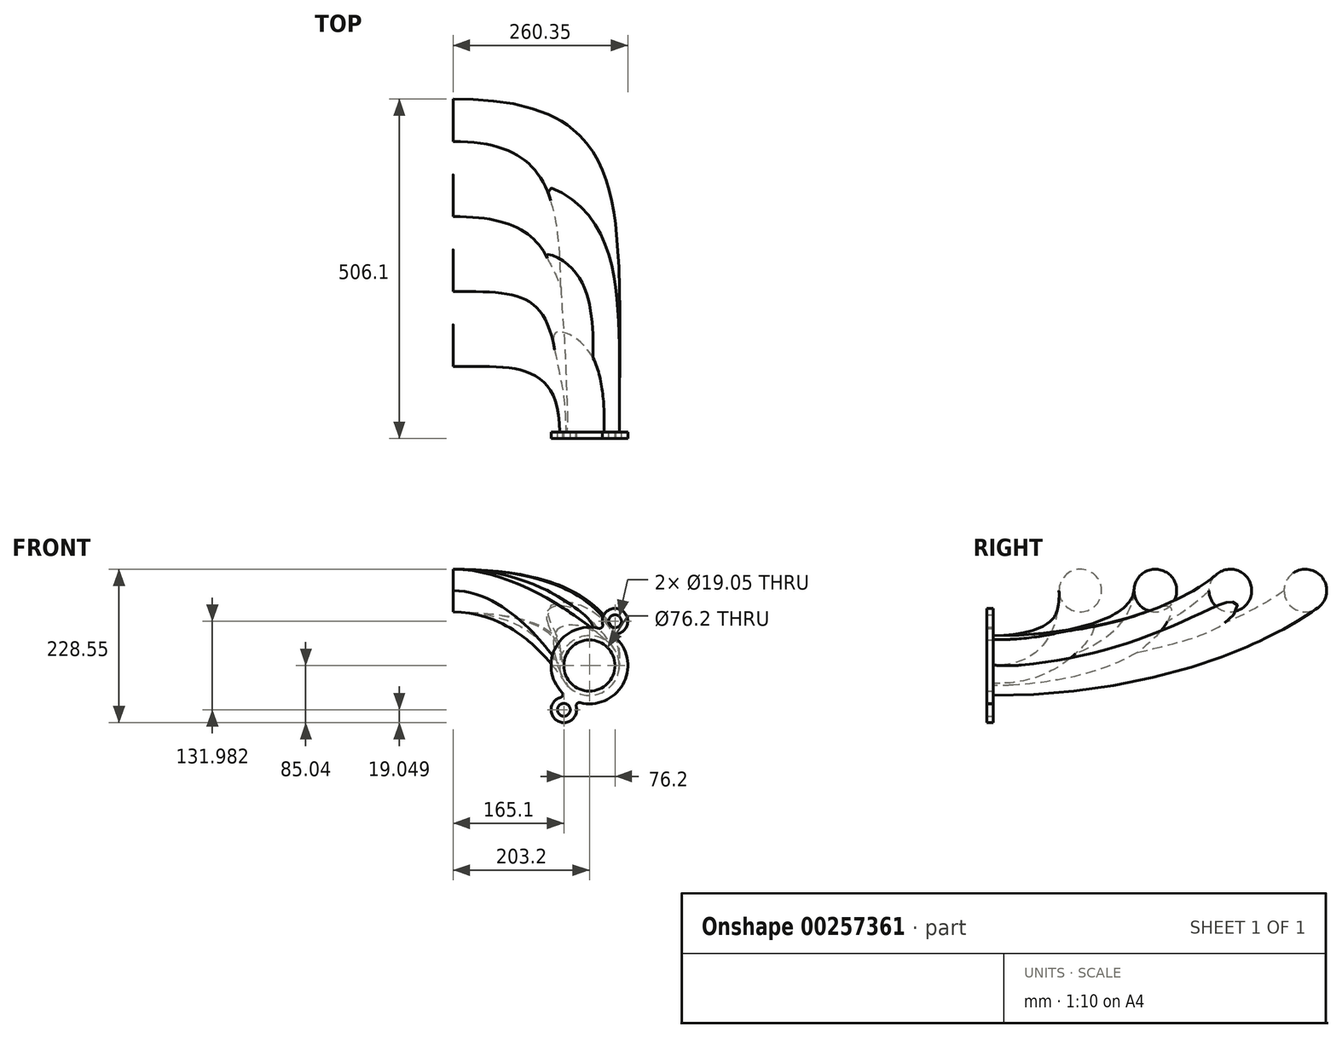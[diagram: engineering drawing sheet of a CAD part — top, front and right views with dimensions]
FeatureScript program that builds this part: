
annotation { "Feature Type Name" : "Feature", "Feature Type Description" : "" }
export const myFeature = defineFeature(function(context is Context, id is Id, definition is map)
    precondition{}
    {
        {
            var Q0;
            Q0=qCreatedBy(makeId("Right.planeOp"),FACE);
            cPlane(context, id + "F0", {"entities" : qUnion([Q0]), "cplaneType" : CPlaneType.OFFSET, "offset" : 203.2 * mm, "oppositeDirection" : true, "width" : 152.4 * mm, "height" : 152.4 * mm});
        }
        {
            var Q0;
            Q0=qCreatedBy(makeId("Top.planeOp"),FACE);
            cPlane(context, id + "F1", {"entities" : qUnion([Q0]), "cplaneType" : CPlaneType.OFFSET, "offset" : 111.76 * mm, "width" : 152.4 * mm, "height" : 152.4 * mm});
        }
        {
            var Q0;
            Q0=qCreatedBy(makeId("Front.planeOp"),FACE);
            var sketch = newSketch(context, id + "F2", { "sketchPlane" : qUnion([Q0])});
            skCircle(sketch, "E0", {"center": v(0, 0) * mm, "radius": 44.45 * mm});
            skLineSegment(sketch, "E1", {"start": v(0, 0) * mm, "end": v(-44.45, 0) * mm, "construction": true});
            skSolve(sketch);
        }
        {
            var Q0;
            Q0=qCreatedBy(id+"F0.planeOp",FACE);
            var sketch = newSketch(context, id + "F3", { "sketchPlane" : qUnion([Q0])});
            skCircle(sketch, "E2", {"center": v(129.54, 111.76) * mm, "radius": 31.75 * mm});
            skCircle(sketch, "E3.1.0.0", {"center": v(241.3, 111.76) * mm, "radius": 31.75 * mm});
            skCircle(sketch, "E3.2.0.0", {"center": v(353.06, 111.76) * mm, "radius": 31.75 * mm});
            skCircle(sketch, "E3.3.0.0", {"center": v(464.82, 111.76) * mm, "radius": 31.75 * mm});
            skLineSegment(sketch, "E3.direction1", {"start": v(129.54, 111.76) * mm, "end": v(241.3, 111.76) * mm, "construction": true});
            skLineSegment(sketch, "E4", {"start": v(97.8, 111.76) * mm, "end": v(129.54, 111.76) * mm, "construction": true});
            skLineSegment(sketch, "E5", {"start": v(353.06, 111.76) * mm, "end": v(321.31, 111.76) * mm, "construction": true});
            skLineSegment(sketch, "E6", {"start": v(464.82, 111.76) * mm, "end": v(433.07, 111.76) * mm, "construction": true});
            skLineSegment(sketch, "E7", {"start": v(241.3, 111.76) * mm, "end": v(209.55, 111.76) * mm, "construction": true});
            skSolve(sketch);
        }
        {
            var Q0;
            Q0=makeQuery(id+"F3.imprint","IMPRINT",FACE,{"disambiguationData":[TD([[makeQuery(id+"F3.imprint","IMPRINT",EDGE,{"derivedFrom":sQuery(id+"F3.wireOp",EDGE,"E2")}),1.0]])]});
            var Q1;
            Q1=makeQuery(id+"F2.imprint","IMPRINT",FACE,{"disambiguationData":[TD([[makeQuery(id+"F2.imprint","IMPRINT",EDGE,{"derivedFrom":sQuery(id+"F2.wireOp",EDGE,"E0")}),1.0]])]});
            var Q2;
            Q2=sQuery(id+"F3.wireOp",VERTEX,"E4.start");
            var Q3;
            Q3=sQuery(id+"F2.wireOp",VERTEX,"E1.end");
            loft(context, id + "F4", {"startCondition" : LoftEndDerivativeType.NORMAL_TO_PROFILE, "startMagnitude" : 1.6, "endCondition" : LoftEndDerivativeType.NORMAL_TO_PROFILE, "endMagnitude" : 2.9, "sheetProfilesArray" : [{ "sheetProfileEntities" : qUnion([Q0]) }, { "sheetProfileEntities" : qUnion([Q1]) }], "matchConnections" : true, "connections" : [{ "connectionEntities" : qUnion([Q2, Q3]), "connectionEdgeQueries" : qUnion([]), "connectionEdgeParameters" : [] }]});
        }
        {
            var Q1;
            Q1=makeQuery(id+"F3.imprint","IMPRINT",FACE,{"disambiguationData":[TD([[makeQuery(id+"F3.imprint","IMPRINT",EDGE,{"derivedFrom":sQuery(id+"F3.wireOp",EDGE,"E3.1.0.0")}),1.0]])]});
            var Q2;
            Q2=makeQuery(id+"F2.imprint","IMPRINT",FACE,{"disambiguationData":[TD([[makeQuery(id+"F2.imprint","IMPRINT",EDGE,{"derivedFrom":sQuery(id+"F2.wireOp",EDGE,"E0")}),1.0]])]});
            var Q3;
            Q3=sQuery(id+"F3.wireOp",VERTEX,"E7.end");
            var Q4;
            Q4=sQuery(id+"F2.wireOp",VERTEX,"E1.end");
            loft(context, id + "F5", {"operationType" : NewBodyOperationType.ADD, "startCondition" : LoftEndDerivativeType.NORMAL_TO_PROFILE, "startMagnitude" : 2.2, "endCondition" : LoftEndDerivativeType.NORMAL_TO_PROFILE, "endMagnitude" : 2.9, "sheetProfilesArray" : [{ "sheetProfileEntities" : qUnion([Q1]) }, { "sheetProfileEntities" : qUnion([Q2]) }], "matchConnections" : true, "connections" : [{ "connectionEntities" : qUnion([Q3, Q4]), "connectionEdgeQueries" : qUnion([]), "connectionEdgeParameters" : [] }]});
        }
        {
            var Q1;
            Q1=makeQuery(id+"F3.imprint","IMPRINT",FACE,{"disambiguationData":[TD([[makeQuery(id+"F3.imprint","IMPRINT",EDGE,{"derivedFrom":sQuery(id+"F3.wireOp",EDGE,"E3.2.0.0")}),1.0]])]});
            var Q2;
            Q2=makeQuery(id+"F2.imprint","IMPRINT",FACE,{"disambiguationData":[TD([[makeQuery(id+"F2.imprint","IMPRINT",EDGE,{"derivedFrom":sQuery(id+"F2.wireOp",EDGE,"E0")}),1.0]])]});
            var Q3;
            Q3=sQuery(id+"F3.wireOp",VERTEX,"E5.end");
            var Q4;
            Q4=sQuery(id+"F2.wireOp",VERTEX,"E1.end");
            loft(context, id + "F6", {"operationType" : NewBodyOperationType.ADD, "startCondition" : LoftEndDerivativeType.NORMAL_TO_PROFILE, "startMagnitude" : 3, "endCondition" : LoftEndDerivativeType.NORMAL_TO_PROFILE, "endMagnitude" : 2, "sheetProfilesArray" : [{ "sheetProfileEntities" : qUnion([Q1]) }, { "sheetProfileEntities" : qUnion([Q2]) }], "matchConnections" : true, "connections" : [{ "connectionEntities" : qUnion([Q3, Q4]), "connectionEdgeQueries" : qUnion([]), "connectionEdgeParameters" : [] }]});
        }
        {
            var Q1;
            Q1=makeQuery(id+"F3.imprint","IMPRINT",FACE,{"disambiguationData":[TD([[makeQuery(id+"F3.imprint","IMPRINT",EDGE,{"derivedFrom":sQuery(id+"F3.wireOp",EDGE,"E3.3.0.0")}),1.0]])]});
            var Q2;
            Q2=makeQuery(id+"F2.imprint","IMPRINT",FACE,{"disambiguationData":[TD([[makeQuery(id+"F2.imprint","IMPRINT",EDGE,{"derivedFrom":sQuery(id+"F2.wireOp",EDGE,"E0")}),1.0]])]});
            var Q3;
            Q3=sQuery(id+"F3.wireOp",VERTEX,"E6.end");
            var Q4;
            Q4=sQuery(id+"F2.wireOp",VERTEX,"E1.end");
            loft(context, id + "F7", {"operationType" : NewBodyOperationType.ADD, "startCondition" : LoftEndDerivativeType.NORMAL_TO_PROFILE, "startMagnitude" : 3, "endCondition" : LoftEndDerivativeType.NORMAL_TO_PROFILE, "endMagnitude" : 2, "sheetProfilesArray" : [{ "sheetProfileEntities" : qUnion([Q1]) }, { "sheetProfileEntities" : qUnion([Q2]) }], "matchConnections" : true, "connections" : [{ "connectionEntities" : qUnion([Q3, Q4]), "connectionEdgeQueries" : qUnion([]), "connectionEdgeParameters" : [] }]});
        }
        {
            var Q0;
            Q0=makeQuery(id+"F2.imprint","IMPRINT",FACE,{"disambiguationData":[TD([[makeQuery(id+"F2.imprint","IMPRINT",EDGE,{"derivedFrom":sQuery(id+"F2.wireOp",EDGE,"E0")}),1.0]])]});
            var sketch = newSketch(context, id + "F8", { "sketchPlane" : qUnion([Q0])});
            skCircle(sketch, "E8", {"center": v(0, 0) * mm, "radius": 38.1 * mm});
            skArc(sketch, "E9", {"start": v(-13.88, -55.44) * mm, "mid": v(49.5, -28.57) * mm, "end": v(41.07, 39.74) * mm});
            skLineSegment(sketch, "E10", {"start": v(0, 0) * mm, "end": v(0, 38.1) * mm, "construction": true});
            skLineSegment(sketch, "E11", {"start": v(0, 0) * mm, "end": v(28.58, 49.5) * mm, "construction": true});
            skArc(sketch, "E12", {"start": v(43.21, 47.64) * mm, "mid": v(47.62, 82.49) * mm, "end": v(19.65, 61.24) * mm});
            skCircle(sketch, "E13", {"center": v(38.1, 66) * mm, "radius": 9.53 * mm});
            skArc(sketch, "E14", {"start": v(43.21, 47.64) * mm, "mid": v(39.9, 44.3) * mm, "end": v(41.07, 39.74) * mm});
            skArc(sketch, "E15.MirrorC", {"start": v(19.65, 61.24) * mm, "mid": v(18.42, 56.7) * mm, "end": v(13.88, 55.44) * mm});
            skLineSegment(sketch, "E16", {"start": v(0, 0) * mm, "end": v(-17.27, 9.97) * mm});
            skArc(sketch, "E17.MirrorC", {"start": v(-19.65, -61.24) * mm, "mid": v(-47.62, -82.49) * mm, "end": v(-43.21, -47.64) * mm});
            skCircle(sketch, "E18.MirrorC", {"center": v(-38.1, -66) * mm, "radius": 9.53 * mm});
            skArc(sketch, "E19.MirrorC", {"start": v(-19.65, -61.24) * mm, "mid": v(-18.42, -56.7) * mm, "end": v(-13.88, -55.44) * mm});
            skArc(sketch, "E20.MirrorC", {"start": v(-43.21, -47.64) * mm, "mid": v(-39.9, -44.3) * mm, "end": v(-41.07, -39.74) * mm});
            skArc(sketch, "E21.trimOffspring", {"start": v(13.88, 55.44) * mm, "mid": v(-49.5, 28.58) * mm, "end": v(-41.07, -39.74) * mm});
            skSolve(sketch);
        }
        {
            var Q0;
            Q0 = qSketchRegion(id + "F8", true);
            extrude(context, id + "F9", {"entities" : qUnion([Q0]), "depth" : 9.52 * mm});
        }
    });
